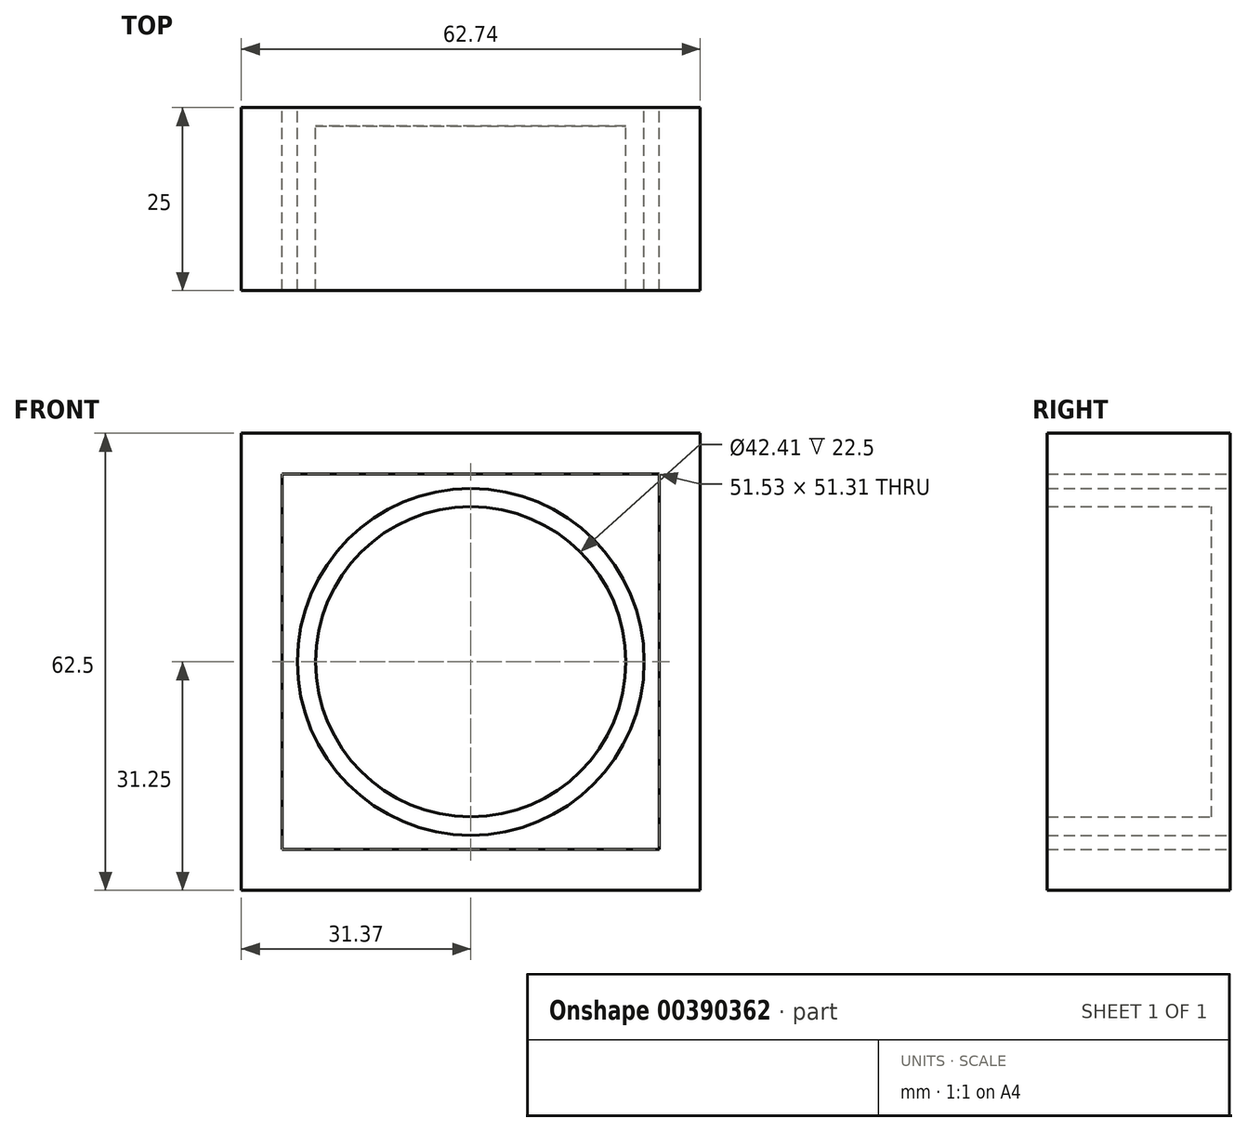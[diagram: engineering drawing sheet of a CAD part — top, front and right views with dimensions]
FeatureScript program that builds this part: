
annotation { "Feature Type Name" : "Feature", "Feature Type Description" : "" }
export const myFeature = defineFeature(function(context is Context, id is Id, definition is map)
    precondition{}
    {
        {
            var Q0;
            Q0=qCreatedBy(makeId("Front.planeOp"),FACE);
            var sketch = newSketch(context, id + "F0", { "sketchPlane" : qUnion([Q0])});
            skCircle(sketch, "E0", {"center": v(0, 0) * mm, "radius": 23.7 * mm});
            skLineSegment(sketch, "E1.bottom", {"start": v(25.76, -25.65) * mm, "end": v(-25.76, -25.65) * mm});
            skLineSegment(sketch, "E1.top", {"start": v(25.76, 25.65) * mm, "end": v(-25.76, 25.65) * mm});
            skLineSegment(sketch, "E1.left", {"start": v(25.76, -25.65) * mm, "end": v(25.76, 25.65) * mm});
            skLineSegment(sketch, "E1.right", {"start": v(-25.76, -25.65) * mm, "end": v(-25.76, 25.65) * mm});
            skLineSegment(sketch, "E2.bottom", {"start": v(31.37, -31.25) * mm, "end": v(-31.37, -31.25) * mm});
            skLineSegment(sketch, "E2.top", {"start": v(31.37, 31.25) * mm, "end": v(-31.37, 31.25) * mm});
            skLineSegment(sketch, "E2.left", {"start": v(31.37, -31.25) * mm, "end": v(31.37, 31.25) * mm});
            skLineSegment(sketch, "E2.right", {"start": v(-31.37, -31.25) * mm, "end": v(-31.37, 31.25) * mm});
            skSolve(sketch);
        }
        {
            var Q0;
            Q0 = qSketchRegion(id + "F0", true);
            var Q1;
            Q1=makeQuery(id+"F0.imprint","IMPRINT",FACE,{"disambiguationData":[TD([[makeQuery(id+"F0.imprint","IMPRINT",EDGE,{"derivedFrom":sQuery(id+"F0.wireOp",EDGE,"E0")}),1.0]])]});
            extrude(context, id + "F1", {"entities" : qUnion([Q0, Q1]), "depth" : 25 * mm});
        }
        {
            var Q0;
            Q0=makeQuery(id+"F1.opExtrude","CAP_FACE",FACE,{"disambiguationData":[OSD([sQuery(id+"F0.wireOp",EDGE,"E0")])],"isStart":false});
            shell(context, id + "F2", {"entities" : qUnion([Q0]), "thickness" : 2.5 * mm});
        }
    });
